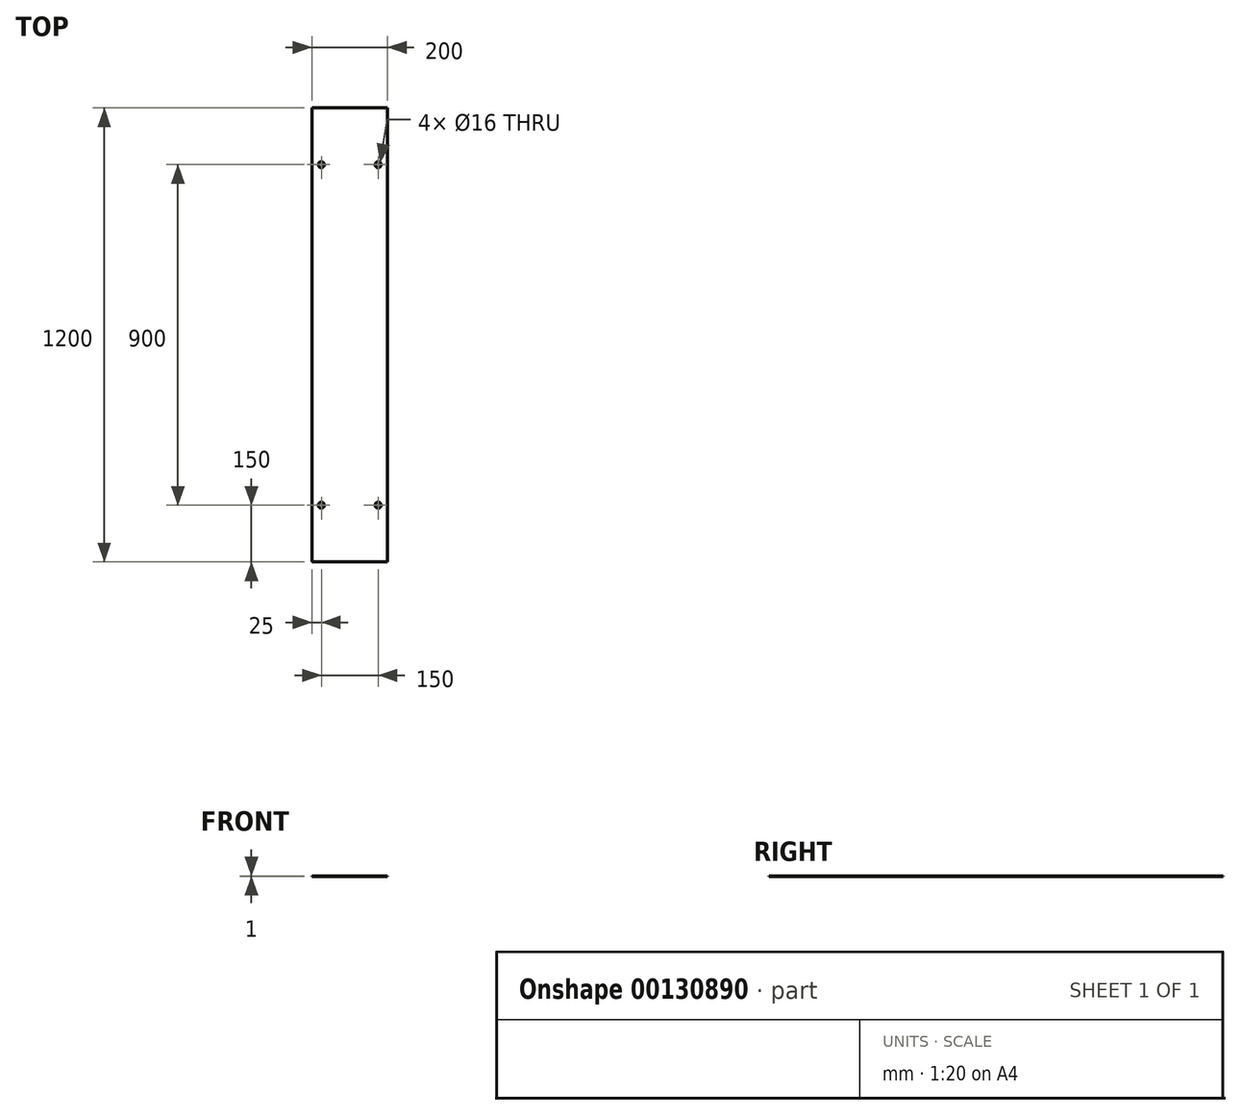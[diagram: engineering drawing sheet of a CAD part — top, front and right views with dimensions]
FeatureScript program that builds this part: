
annotation { "Feature Type Name" : "Feature", "Feature Type Description" : "" }
export const myFeature = defineFeature(function(context is Context, id is Id, definition is map)
    precondition{}
    {
        {
            var Q0;
            Q0=qCreatedBy(makeId("Top.planeOp"),FACE);
            var sketch = newSketch(context, id + "F0", { "sketchPlane" : qUnion([Q0])});
            skLineSegment(sketch, "E0.bottom", {"start": v(0, 0) * mm, "end": v(200, 0) * mm});
            skLineSegment(sketch, "E0.top", {"start": v(0, 1200) * mm, "end": v(200, 1200) * mm});
            skLineSegment(sketch, "E0.left", {"start": v(0, 0) * mm, "end": v(0, 1200) * mm});
            skLineSegment(sketch, "E0.right", {"start": v(200, 0) * mm, "end": v(200, 1200) * mm});
            skCircle(sketch, "E1", {"center": v(175, 150) * mm, "radius": 8 * mm});
            skCircle(sketch, "E2.MirrorC", {"center": v(175, 1050) * mm, "radius": 8 * mm});
            skCircle(sketch, "E3.MirrorC", {"center": v(25, 150) * mm, "radius": 8 * mm});
            skCircle(sketch, "E4.MirrorC", {"center": v(25, 1050) * mm, "radius": 8 * mm});
            skSolve(sketch);
        }
        {
            var Q0;
            Q0 = qSketchRegion(id + "F0", true);
            extrude(context, id + "F1", {"entities" : qUnion([Q0]), "depth" : 1 * mm});
        }
    });
